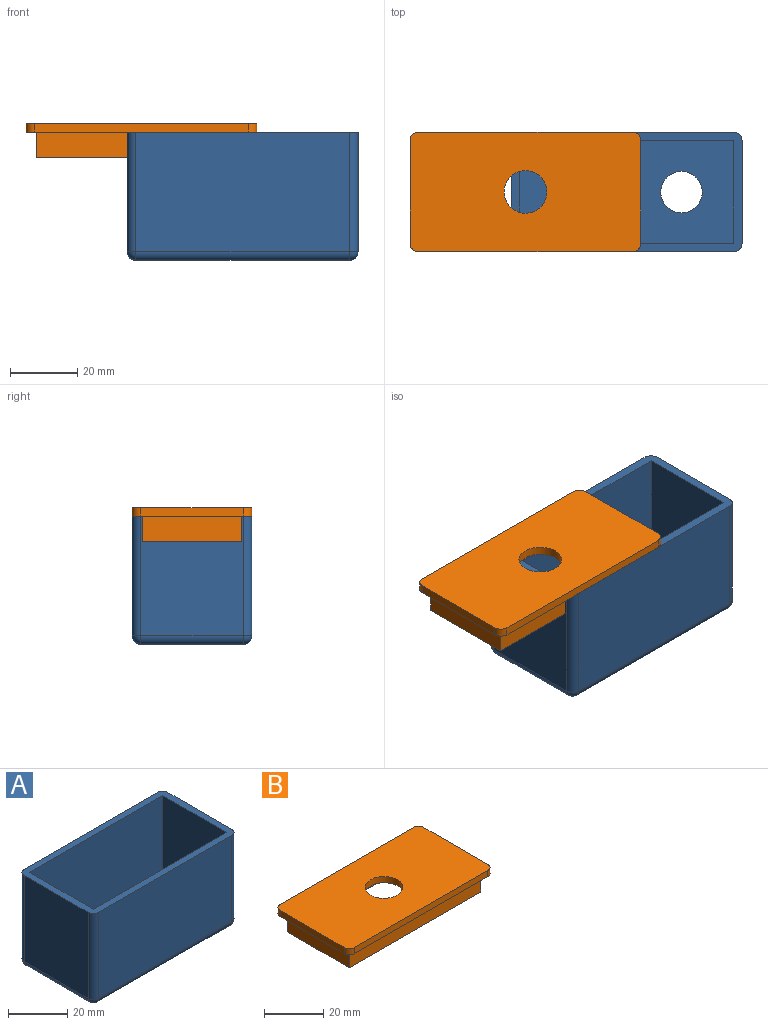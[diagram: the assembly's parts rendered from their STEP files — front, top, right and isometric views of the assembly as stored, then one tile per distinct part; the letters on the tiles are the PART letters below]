
ASSEMBLY  parts=2 mates=1
PART A: 25 faces, bbox 68.6x35.6x38.1 mm
  f0: plane 35.56x30.48mm, normal (-1,0,0), area 1083.9mm2, adj f8,f18,f22,f24
  f1: plane 63.5x35.56mm, normal (0,-1,0), area 2258.1mm2, adj f8,f15,f21,f24
  f2: plane 35.56x30.48mm, normal (1,0,0), area 1083.9mm2, adj f8,f13,f15,f16
  f3: plane 35.56x30.48mm, normal (-1,0,0), area 1083.9mm2, adj f4,f6,f8,f10
  f4: plane 63.5x35.56mm, normal (0,1,0), area 2258.1mm2, adj f3,f5,f8,f10
  f5: plane 35.56x30.48mm, normal (1,0,0), area 1083.9mm2, adj f4,f6,f8,f10
  f6: plane 63.5x35.56mm, normal (0,-1,0), area 2258.1mm2, adj f3,f5,f8,f10
  f7: plane 63.5x35.56mm, normal (0,1,0), area 2258.1mm2, adj f8,f13,f17,f18
  f8: plane 68.58x35.56mm, normal (0,0,1), area 497.7mm2, adj f0,f1,f2,f3,f4,f5,f6,f7
  f9: plane 63.5x30.48mm, normal (0,0,-1), area 1697.1mm2, adj f11,f12,f16,f17,f21,f22
  f10: plane 63.5x30.48mm, normal (0,0,1), area 1697.1mm2, adj f3,f4,f5,f6,f11,f12
  f11: cylinder r=6.16mm len=12.32mm, axis (0,0,-1), area 98.3mm2, adj f9,f10
  f12: cylinder r=6.16mm len=12.32mm, axis (0,0,-1), area 98.3mm2, adj f9,f10
  f13: cylinder r=2.54mm len=35.56mm, axis (0,0,-1), area 141.9mm2, adj f2,f7,f8,f14
  f14: sphere r=2.54mm, area 10.1mm2, adj f13,f16,f17
  f15: cylinder r=2.54mm len=35.56mm, axis (0,0,1), area 141.9mm2, adj f1,f2,f8,f19
  f16: cylinder r=2.54mm len=30.48mm, axis (0,1,0), area 121.6mm2, adj f2,f9,f14,f19
  f17: cylinder r=2.54mm len=63.5mm, axis (-1,0,0), area 253.4mm2, adj f7,f9,f14,f20
  f18: cylinder r=2.54mm len=35.56mm, axis (0,0,1), area 141.9mm2, adj f0,f7,f8,f20
  f19: sphere r=2.54mm, area 10.1mm2, adj f15,f16,f21
  f20: sphere r=2.54mm, area 10.1mm2, adj f17,f18,f22
  f21: cylinder r=2.54mm len=63.5mm, axis (1,0,0), area 253.4mm2, adj f1,f9,f19,f23
  f22: cylinder r=2.54mm len=30.48mm, axis (0,-1,0), area 121.6mm2, adj f0,f9,f20,f23
  f23: sphere r=2.54mm, area 10.1mm2, adj f21,f22,f24
  f24: cylinder r=2.54mm len=35.56mm, axis (0,0,-1), area 141.9mm2, adj f0,f1,f8,f23
PART B: 21 faces, bbox 68.6x35.6x10.2 mm
  f0: plane 60.05x7.62mm, normal (0,1,0), area 457.5mm2, adj f1,f7,f8,f9
  f1: plane 27.03x7.62mm, normal (1,0,0), area 205.9mm2, adj f0,f2,f8,f9
  f2: plane 60.05x7.62mm, normal (0,-1,0), area 457.5mm2, adj f1,f7,f8,f9
  f3: plane 29.57x7.62mm, normal (-1,0,0), area 225.3mm2, adj f4,f6,f8,f19
  f4: plane 62.59x7.62mm, normal (0,-1,0), area 476.9mm2, adj f3,f5,f8,f19
  f5: plane 29.57x7.62mm, normal (1,0,0), area 225.3mm2, adj f4,f6,f8,f19
  f6: plane 62.59x7.62mm, normal (0,1,0), area 476.9mm2, adj f3,f5,f8,f19
  f7: plane 27.03x7.62mm, normal (-1,0,0), area 205.9mm2, adj f0,f2,f8,f9
  f8: plane 62.59x29.57mm, normal (0,0,-1), area 227.6mm2, adj f0,f1,f2,f3,f4,f5,f6,f7
  f9: plane 60.05x27.03mm, normal (0,0,-1), area 1496.1mm2, adj f0,f1,f2,f7,f20
  f10: plane 63.5x2.54mm, normal (0,-1,0), area 161.3mm2, adj f11,f17,f18,f19
  f11: cylinder r=2.54mm len=2.54mm, axis (0,0,-1), area 10.1mm2, adj f10,f12,f18,f19
  f12: plane 30.48x2.54mm, normal (1,0,0), area 77.4mm2, adj f11,f13,f18,f19
  f13: cylinder r=2.54mm len=2.54mm, axis (0,0,-1), area 10.1mm2, adj f12,f14,f18,f19
  f14: plane 63.5x2.54mm, normal (0,1,0), area 161.3mm2, adj f13,f15,f18,f19
  f15: cylinder r=2.54mm len=2.54mm, axis (0,0,-1), area 10.1mm2, adj f14,f16,f18,f19
  f16: plane 30.48x2.54mm, normal (-1,0,0), area 77.4mm2, adj f15,f17,f18,f19
  f17: cylinder r=2.54mm len=2.54mm, axis (0,0,-1), area 10.1mm2, adj f10,f16,f18,f19
  f18: plane 68.58x35.56mm, normal (0,0,1), area 2306.5mm2, adj f10,f11,f12,f13,f14,f15,f16,f17
  f19: plane 68.58x35.56mm, normal (0,0,-1), area 582.8mm2, adj f3,f4,f5,f6,f10,f11,f12,f13
  f20: cylinder r=6.35mm len=12.7mm, axis (0,0,1), area 101.3mm2, adj f9,f18
PLACE A t=(-5,4.68,-7.7)mm
PLACE B t=(-35.03,4.68,-7.7)mm
MATE fastened B.f9 <-> A.f8  axis (0,0,-1) through (-5,4.68,30.4)mm
